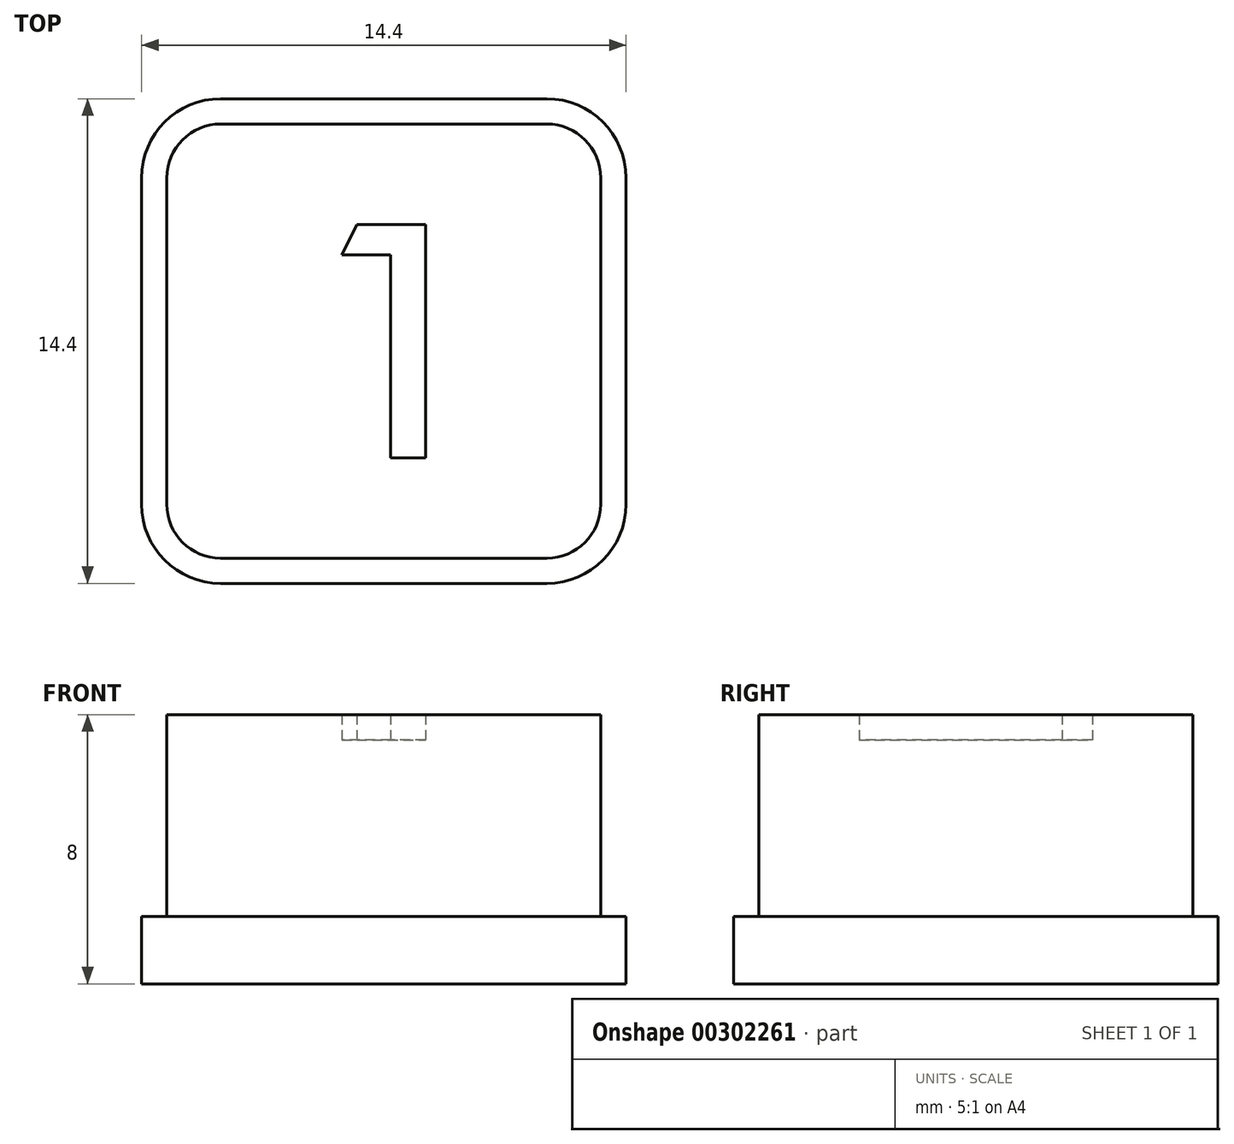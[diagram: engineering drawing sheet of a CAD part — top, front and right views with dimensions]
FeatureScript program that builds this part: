
annotation { "Feature Type Name" : "Feature", "Feature Type Description" : "" }
export const myFeature = defineFeature(function(context is Context, id is Id, definition is map)
    precondition{}
    {
        {
            var Q0;
            Q0=qCreatedBy(makeId("Top.planeOp"),FACE);
            var sketch = newSketch(context, id + "F0", { "sketchPlane" : qUnion([Q0])});
            skLineSegment(sketch, "E0", {"start": v(0.2, -3.47) * mm, "end": v(0.2, 2.57) * mm});
            skLineSegment(sketch, "E1", {"start": v(0.2, 2.57) * mm, "end": v(-1.24, 2.57) * mm});
            skLineSegment(sketch, "E2", {"start": v(-1.24, 2.57) * mm, "end": v(-0.8, 3.47) * mm});
            skLineSegment(sketch, "E3", {"start": v(-0.8, 3.47) * mm, "end": v(1.24, 3.47) * mm});
            skLineSegment(sketch, "E4", {"start": v(1.24, 3.47) * mm, "end": v(1.24, -3.47) * mm});
            skLineSegment(sketch, "E5", {"start": v(1.24, -3.47) * mm, "end": v(0.2, -3.47) * mm});
            skArc(sketch, "E6", {"start": v(4.85, -6.45) * mm, "mid": v(5.98, -5.98) * mm, "end": v(6.45, -4.85) * mm});
            skLineSegment(sketch, "E7", {"start": v(6.45, -4.85) * mm, "end": v(6.45, 4.85) * mm});
            skArc(sketch, "E8", {"start": v(6.45, 4.85) * mm, "mid": v(5.98, 5.98) * mm, "end": v(4.85, 6.45) * mm});
            skLineSegment(sketch, "E9", {"start": v(4.85, 6.45) * mm, "end": v(-4.85, 6.45) * mm});
            skArc(sketch, "E10", {"start": v(-4.85, 6.45) * mm, "mid": v(-5.98, 5.98) * mm, "end": v(-6.45, 4.85) * mm});
            skLineSegment(sketch, "E11", {"start": v(-6.45, 4.85) * mm, "end": v(-6.45, -4.85) * mm});
            skArc(sketch, "E12", {"start": v(-6.45, -4.85) * mm, "mid": v(-5.98, -5.98) * mm, "end": v(-4.85, -6.45) * mm});
            skLineSegment(sketch, "E13", {"start": v(-4.85, -6.45) * mm, "end": v(4.85, -6.45) * mm});
            skArc(sketch, "E14", {"start": v(-4.85, 7.2) * mm, "mid": v(-6.51, 6.51) * mm, "end": v(-7.2, 4.85) * mm});
            skLineSegment(sketch, "E15", {"start": v(-7.2, 4.85) * mm, "end": v(-7.2, -4.85) * mm});
            skArc(sketch, "E16", {"start": v(-7.2, -4.85) * mm, "mid": v(-6.51, -6.51) * mm, "end": v(-4.85, -7.2) * mm});
            skLineSegment(sketch, "E17", {"start": v(-4.85, -7.2) * mm, "end": v(4.85, -7.2) * mm});
            skArc(sketch, "E18", {"start": v(4.85, -7.2) * mm, "mid": v(6.51, -6.51) * mm, "end": v(7.2, -4.85) * mm});
            skLineSegment(sketch, "E19", {"start": v(7.2, -4.85) * mm, "end": v(7.2, 4.85) * mm});
            skArc(sketch, "E20", {"start": v(7.2, 4.85) * mm, "mid": v(6.51, 6.51) * mm, "end": v(4.85, 7.2) * mm});
            skLineSegment(sketch, "E21", {"start": v(4.85, 7.2) * mm, "end": v(-4.85, 7.2) * mm});
            skSolve(sketch);
        }
        {
            var Q0;
            Q0 = qSketchRegion(id + "F0", true);
            extrude(context, id + "F1", {"entities" : qUnion([Q0]), "depth" : 2 * mm});
        }
        {
            var Q0;
            Q0=makeQuery(id+"F0.imprint","IMPRINT",FACE,{"disambiguationData":[TD([[makeQuery(id+"F0.imprint","IMPRINT",EDGE,{"derivedFrom":sQuery(id+"F0.wireOp",EDGE,"E0")}),1.0]])]});
            extrude(context, id + "F2", {"entities" : qUnion([Q0]), "operationType" : NewBodyOperationType.ADD, "depth" : 8 * mm});
        }
        {
            var Q0;
            Q0=makeQuery(id+"F0.imprint","IMPRINT",FACE,{"disambiguationData":[TD([[makeQuery(id+"F0.imprint","IMPRINT",EDGE,{"derivedFrom":sQuery(id+"F0.wireOp",EDGE,"E0")}),-1.0]])]});
            extrude(context, id + "F3", {"entities" : qUnion([Q0]), "operationType" : NewBodyOperationType.ADD, "depth" : 7.25 * mm});
        }
    });
